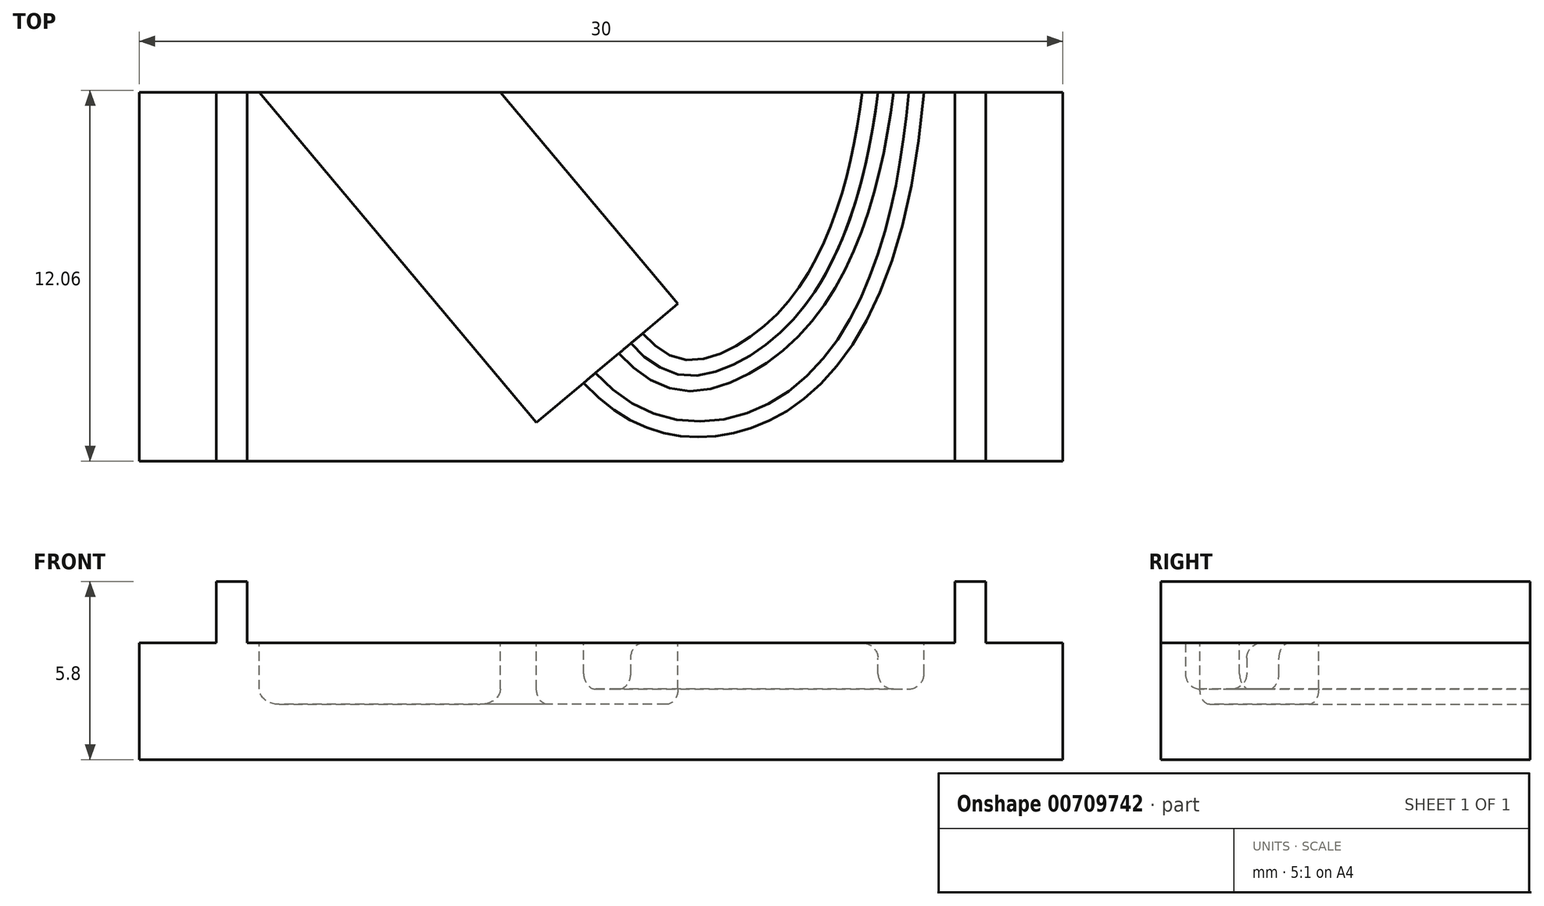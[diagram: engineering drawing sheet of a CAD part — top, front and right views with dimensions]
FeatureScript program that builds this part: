
annotation { "Feature Type Name" : "Feature", "Feature Type Description" : "" }
export const myFeature = defineFeature(function(context is Context, id is Id, definition is map)
    precondition{}
    {
        {
            var Q0;
            Q0=qCreatedBy(makeId("Top.planeOp"),FACE);
            var sketch = newSketch(context, id + "F0", { "sketchPlane" : qUnion([Q0])});
            skLineSegment(sketch, "E0.bottom", {"start": v(0, 0) * mm, "end": v(30, 0) * mm});
            skLineSegment(sketch, "E0.top", {"start": v(0, -12) * mm, "end": v(30, -12) * mm});
            skLineSegment(sketch, "E0.left", {"start": v(0, 0) * mm, "end": v(0, -12) * mm});
            skLineSegment(sketch, "E0.right", {"start": v(30, 0) * mm, "end": v(30, -12) * mm});
            skSolve(sketch);
        }
        {
            var Q0;
            Q0 = qSketchRegion(id + "F0", true);
            extrude(context, id + "F1", {"entities" : qUnion([Q0]), "depth" : 3.8 * mm, "offsetDistance" : 25 * mm});
        }
        {
            var Q0;
            Q0=makeQuery(id+"F1.opExtrude","CAP_FACE",FACE,{"disambiguationData":[OSD([sQuery(id+"F0.wireOp",EDGE,"E0.bottom"),sQuery(id+"F0.wireOp",EDGE,"E0.top"),sQuery(id+"F0.wireOp",EDGE,"E0.left"),sQuery(id+"F0.wireOp",EDGE,"E0.right")])],"isStart":false});
            var sketch = newSketch(context, id + "F2", { "sketchPlane" : qUnion([Q0])});
            skLineSegment(sketch, "E1.bottom", {"start": v(2.5, 0) * mm, "end": v(3.5, 0) * mm});
            skLineSegment(sketch, "E1.top", {"start": v(2.5, -12) * mm, "end": v(3.5, -12) * mm});
            skLineSegment(sketch, "E1.left", {"start": v(2.5, 0) * mm, "end": v(2.5, -12) * mm});
            skLineSegment(sketch, "E1.right", {"start": v(3.5, 0) * mm, "end": v(3.5, -12) * mm});
            skLineSegment(sketch, "E2.bottom", {"start": v(26.5, 0) * mm, "end": v(27.5, 0) * mm});
            skLineSegment(sketch, "E2.top", {"start": v(26.5, -12) * mm, "end": v(27.5, -12) * mm});
            skLineSegment(sketch, "E2.left", {"start": v(26.5, 0) * mm, "end": v(26.5, -12) * mm});
            skLineSegment(sketch, "E2.right", {"start": v(27.5, 0) * mm, "end": v(27.5, -12) * mm});
            skLineSegment(sketch, "E3", {"start": v(2.5, 0) * mm, "end": v(27.5, 0) * mm, "construction": true});
            skLineSegment(sketch, "E4", {"start": v(17.5, -9.88) * mm, "end": v(17.5, -6.88) * mm, "construction": true});
            skLineSegment(sketch, "E5", {"start": v(17.5, -6.88) * mm, "end": v(11.73, 0) * mm});
            skLineSegment(sketch, "E6", {"start": v(17.5, -6.88) * mm, "end": v(19.8, -4.95) * mm});
            skLineSegment(sketch, "E7", {"start": v(17.5, -6.88) * mm, "end": v(12.9, -10.74) * mm});
            skLineSegment(sketch, "E8", {"start": v(12.9, -10.74) * mm, "end": v(3.5, 0.47) * mm});
            skLineSegment(sketch, "E9", {"start": v(11.73, 0) * mm, "end": v(3.9, 0) * mm});
            skLineSegment(sketch, "E10", {"start": v(12.9, -10.74) * mm, "end": v(14.44, -9.45) * mm, "construction": true});
            skLineSegment(sketch, "E11", {"start": v(15.97, -8.17) * mm, "end": v(17.5, -6.88) * mm, "construction": true});
            skLineSegment(sketch, "E12", {"start": v(26.5, 0) * mm, "end": v(25.5, 0) * mm, "construction": true});
            skLineSegment(sketch, "E13", {"start": v(25.5, 0) * mm, "end": v(24, 0) * mm, "construction": true});
            skLineSegment(sketch, "E14", {"start": v(24, 0) * mm, "end": v(22.66, 0) * mm, "construction": true});
            skFitSpline(sketch, "E15", {"points": [v(15.97, -8.17) * mm, v(19.36, -8.82) * mm, v(24, 0) * mm], "startDerivative": vector(9.7, -10.83) * mm, "endDerivative": vector(3.41, 27.24) * mm});
            skFitSpline(sketch, "E16", {"points": [v(14.44, -9.45) * mm, v(19.25, -11.09) * mm, v(25.5, 0) * mm], "startDerivative": vector(11.06, -12) * mm, "endDerivative": vector(3.3, 38.23) * mm});
            skLineSegment(sketch, "E17", {"start": v(3.5, -11) * mm, "end": v(17.5, -11) * mm, "construction": true});
            skSolve(sketch);
        }
        {
            var Q0;
            Q0=makeQuery(id+"F2.imprint","IMPRINT",FACE,{"disambiguationData":[TD([[makeQuery(id+"F2.imprint","IMPRINT",EDGE,{"derivedFrom":sQuery(id+"F2.wireOp",EDGE,"E1.bottom")}),-1.0]])]});
            var Q1;
            Q1=makeQuery(id+"F2.imprint","IMPRINT",FACE,{"disambiguationData":[TD([[makeQuery(id+"F2.imprint","IMPRINT",EDGE,{"derivedFrom":sQuery(id+"F2.wireOp",EDGE,"E2.bottom")}),-1.0]])]});
            extrude(context, id + "F3", {"entities" : qUnion([Q0, Q1]), "operationType" : NewBodyOperationType.ADD, "depth" : 2 * mm, "offsetDistance" : 25 * mm});
        }
        {
            var Q0;
            Q0=makeQuery(id+"F2.imprint","IMPRINT",FACE,{"disambiguationData":[TD([[makeQuery(id+"F2.imprint","IMPRINT",EDGE,{"derivedFrom":sQuery(id+"F2.wireOp",EDGE,"E5")}),1.0]])]});
            extrude(context, id + "F4", {"entities" : qUnion([Q0]), "operationType" : NewBodyOperationType.REMOVE, "oppositeDirection" : true, "depth" : 2 * mm, "offsetDistance" : 25 * mm});
        }
        {
            var Q0;
            {var subQ0=sQuery(id+"F2.wireOp",EDGE,"E15");Q0=makeQuery(id+"F2.imprint","IMPRINT",FACE,{"disambiguationData":[TD([[makeQuery(id+"F2.imprint","IMPRINT",EDGE,{"derivedFrom":subQ0}),-1.0]])]});}
            extrude(context, id + "F5", {"entities" : qUnion([Q0]), "operationType" : NewBodyOperationType.REMOVE, "oppositeDirection" : true, "depth" : 1.5 * mm, "offsetDistance" : 25 * mm});
        }
        {
            var Q0;
            Q0=makeQuery(id+"F5.boolean.opBoolean","COPY",EDGE,{"derivedFrom":makeQuery(id+"F5.opExtrude","CAP_EDGE",EDGE,{"disambiguationData":[OSD([sQuery(id+"F2.wireOp",EDGE,"E15")])],"isStart":false})});
            var Q1;
            Q1=makeQuery(id+"F5.boolean.opBoolean","COPY",EDGE,{"derivedFrom":makeQuery(id+"F5.opExtrude","CAP_EDGE",EDGE,{"disambiguationData":[OSD([sQuery(id+"F2.wireOp",EDGE,"E16")])],"isStart":false})});
            var Q2;
            Q2=makeQuery(id+"F4.boolean.opBoolean","COPY",EDGE,{"derivedFrom":makeQuery(id+"F4.opExtrude","CAP_EDGE",EDGE,{"disambiguationData":[OSD([sQuery(id+"F2.wireOp",EDGE,"E5")])],"isStart":false})});
            var Q3;
            Q3=makeQuery(id+"F4.boolean.opBoolean","COPY",EDGE,{"derivedFrom":makeQuery(id+"F4.opExtrude","CAP_EDGE",EDGE,{"disambiguationData":[OSD([sQuery(id+"F2.wireOp",EDGE,"E8")])],"isStart":false})});
            var Q4;
            Q4=makeQuery(id+"F5.boolean.opBoolean","COPY",EDGE,{"derivedFrom":makeQuery(id+"F5.opExtrude","CAP_EDGE",EDGE,{"disambiguationData":[OSD([sQuery(id+"F2.wireOp",EDGE,"E15")])],"isStart":true})});
            var Q5;
            Q5=makeQuery(id+"F5.boolean.opBoolean","COPY",EDGE,{"derivedFrom":makeQuery(id+"F5.opExtrude","CAP_EDGE",EDGE,{"disambiguationData":[OSD([sQuery(id+"F2.wireOp",EDGE,"E16")])],"isStart":true})});
            var Q6;
            Q6=makeQuery(id+"F5.boolean.opBoolean","COPY",EDGE,{"derivedFrom":makeQuery(id+"F5.opExtrude","SWEPT_EDGE",EDGE,{"disambiguationData":[OSD([sQuery(id+"F2.wireOp",EDGE,"E7"),sQuery(id+"F2.wireOp",EDGE,"E15")])]})});
            fillet(context, id + "F6", {"entities" : qUnion([Q0, Q1, Q2, Q3, Q4, Q5, Q6]), "radius" : .5 * mm, "tangentPropagation" : true, "allowEdgeOverflow" : false});
        }
    });
